# Revit family: QF_BOURGEAT_tables_de_tri_standards_2TVO
name_source: partatom
category: Equipement spécialisé
revit_build: Autodesk Revit 2015 (Build: 20140606_1530(x64)
units: mm (PartAtom-declared; Revit-internal decimal feet)

## types (6) — shared parameters
Fabricant = BOURGEAT
Hauteur hors tout = 850 mm  [stored 2.78871 ft]
Inox = Acier inoxydable, poli
Panneaux = PVC, non plastifié
Spécification du Fabricant = Table de collecte et de tri standards
URL catalogue = http://www.bourgeat.fr

## per-type parameters (varying)
| type | Avec panneaux | Décalage du sol | Longueur hors tout | Modèle | Pieds | Poids net à vide | Profondeur hors tout | Rampe | Roulettes |
| Sans rampe - Sans panneaux - Avec pieds | Non | 27 mm  [stored 0.0885827 ft] | 1030 mm  [stored 3.37927 ft] | 858002 | Oui | 29.00 kg | 600 mm | Non | Non |
| Sans rampe - Sans panneaux - Avec roues | Non | 184 mm  [stored 0.603675 ft] | 1060 mm  [stored 3.47769 ft] | 858012 | Non | 29.00 kg | 630 mm  [stored 2.06693 ft] | Non | Oui |
| Avec rampe - Sans panneaux - Avec roues | Non | 184 mm  [stored 0.603675 ft] | 1060 mm  [stored 3.47769 ft] | 858032 | Non | 32.00 kg | 865 mm  [stored 2.83793 ft] | Oui | Oui |
| Avec rampe - Sans panneaux - Avec pieds | Non | 27 mm  [stored 0.0885827 ft] | 1030 mm  [stored 3.37927 ft] | 858022 | Oui | 32.00 kg | 850 mm  [stored 2.78871 ft] | Oui | Non |
| Avec rampe - Avec panneaux - Avec pieds | Oui | 27 mm  [stored 0.0885827 ft] | 1030 mm  [stored 3.37927 ft] | 858102 | Oui | 32.00 kg | 850 mm  [stored 2.78871 ft] | Oui | Non |
| Avec rampe - Avec Panneaux - Avec roues | Oui | 184 mm  [stored 0.603675 ft] | 1060 mm  [stored 3.47769 ft] | 858112 | Non | 32.00 kg | 865 mm  [stored 2.83793 ft] | Oui | Oui |

note: [stored X ft] marks values corroborated as IEEE doubles in the binary element streams (Revit-internal decimal feet)

## geometry (parser evidence)
native form markers: Blend x12
no freeform markers — native parametric forms only
